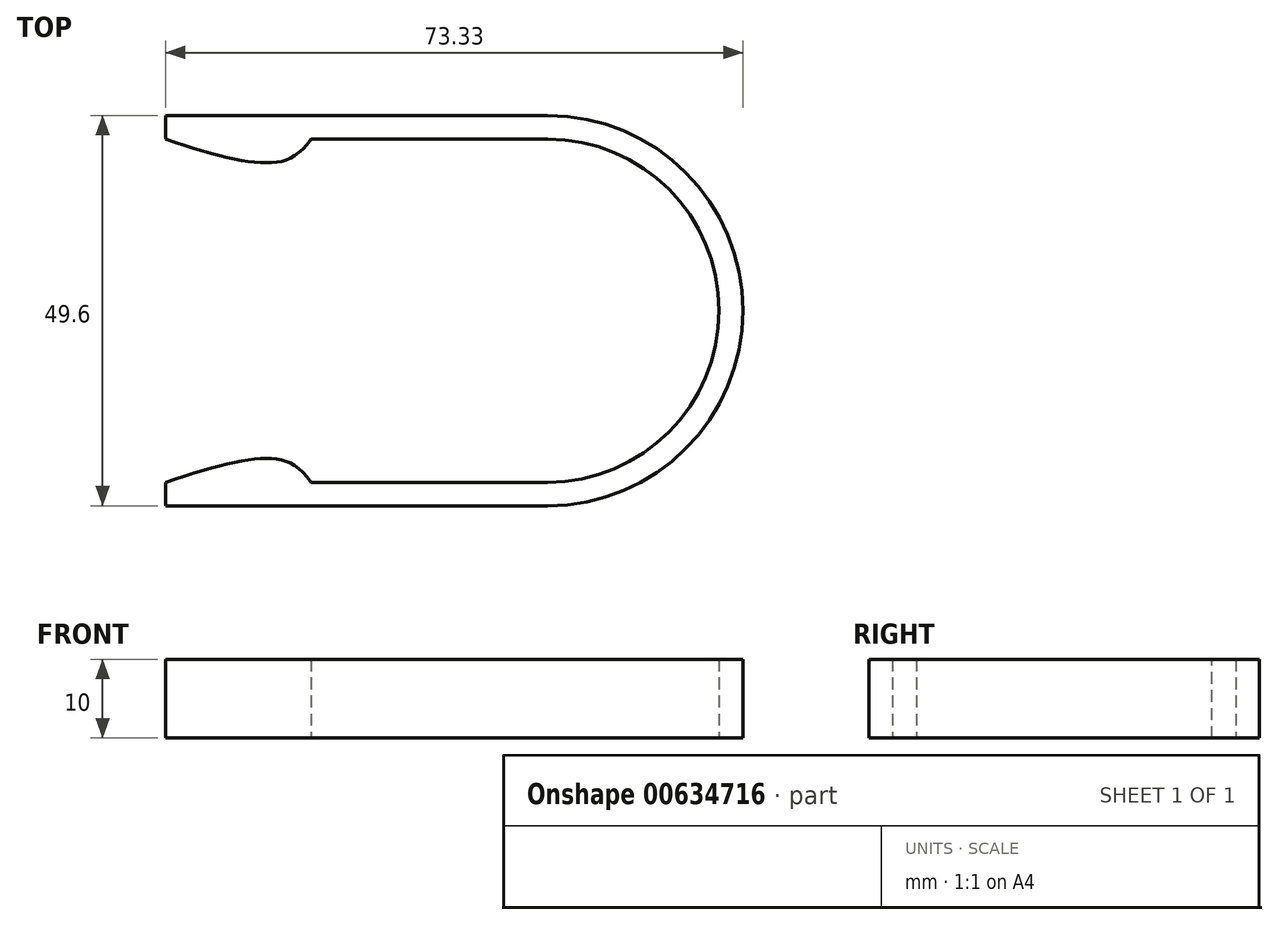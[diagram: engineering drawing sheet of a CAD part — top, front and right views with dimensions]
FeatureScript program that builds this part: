
annotation { "Feature Type Name" : "Feature", "Feature Type Description" : "" }
export const myFeature = defineFeature(function(context is Context, id is Id, definition is map)
    precondition{}
    {
        {
            var Q0;
            Q0=qCreatedBy(makeId("Top.planeOp"),FACE);
            var sketch = newSketch(context, id + "F0", { "sketchPlane" : qUnion([Q0])});
            skLineSegment(sketch, "E0", {"start": v(0, -21.8) * mm, "end": v(30, -21.8) * mm});
            skFitSpline(sketch, "E1", {"points": [v(0, -21.8) * mm, v(-5.13, -18.8) * mm, v(-18.5, -21.8) * mm], "startDerivative": vector(-12.34, 17.1) * mm, "endDerivative": vector(-29.66, -10.14) * mm});
            skLineSegment(sketch, "E2", {"start": v(30.03, -24.8) * mm, "end": v(0, -24.8) * mm});
            skLineSegment(sketch, "E3", {"start": v(0, -24.8) * mm, "end": v(-18.5, -24.8) * mm});
            skLineSegment(sketch, "E4", {"start": v(-18.5, -24.8) * mm, "end": v(-18.5, -21.8) * mm});
            skLineSegment(sketch, "E5", {"start": v(0, 0) * mm, "end": v(39.38, 0) * mm, "construction": true});
            skLineSegment(sketch, "E6.MirrorCS", {"start": v(0, 24.8) * mm, "end": v(-18.5, 24.8) * mm});
            skLineSegment(sketch, "E7.MirrorCS", {"start": v(30.03, 24.8) * mm, "end": v(0, 24.8) * mm});
            skFitSpline(sketch, "E8.MirrorCS", {"points": [v(0, 21.8) * mm, v(-5.13, 18.8) * mm, v(-18.5, 21.8) * mm], "startDerivative": vector(-12.34, -17.1) * mm, "endDerivative": vector(-29.66, 10.14) * mm});
            skLineSegment(sketch, "E9.MirrorCS", {"start": v(-18.5, 24.8) * mm, "end": v(-18.5, 21.8) * mm});
            skLineSegment(sketch, "E10.MirrorCS", {"start": v(0, 21.8) * mm, "end": v(30, 21.8) * mm});
            skArc(sketch, "E11", {"start": v(30, -21.8) * mm, "mid": v(51.8, 0) * mm, "end": v(30, 21.8) * mm});
            skArc(sketch, "E12", {"start": v(30.03, -24.8) * mm, "mid": v(54.83, 0) * mm, "end": v(30.03, 24.8) * mm});
            skSolve(sketch);
        }
        {
            var Q0;
            Q0 = qSketchRegion(id + "F0", true);
            extrude(context, id + "F1", {"entities" : qUnion([Q0]), "depth" : 10 * mm, "offsetDistance" : 25 * mm});
        }
    });
